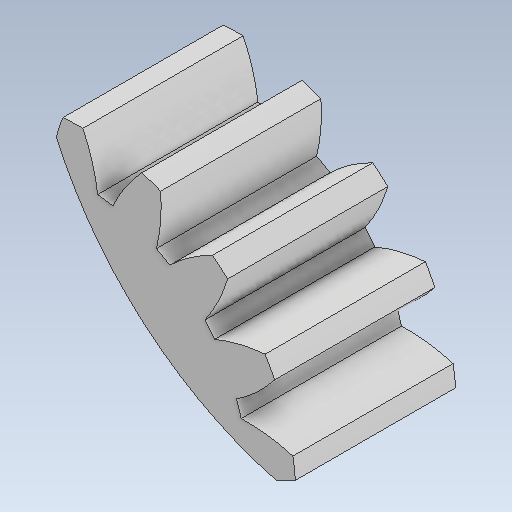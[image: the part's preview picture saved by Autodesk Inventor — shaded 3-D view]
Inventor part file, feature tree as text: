
AUTODESK INVENTOR PART (.ipt)
format: ipt  version: 2020 (Build 240168000, 168)  size: 285,696 bytes
history: native  units: mm
features: other x8, extrude x4, reference x4, sketch x3
ambient origin geometry x8: Origin, YZ Plane, XZ Plane, XY Plane, X Axis, Y Axis, Z Axis, Center Point
bodies: Body1 (feature_tree)
feature tree (19):
  other  "Bryła1"
  sketch  "Szkic1"
  extrude  "Wyciągnięcie proste1"  Depth=30.0mm
  extrude  "Wyciągnięcie proste2"  Depth=3.0mm TaperAngle=0.0deg
  extrude  "Wyciągnięcie proste3"  Depth=0.25mm
  extrude  "Wyciągnięcie proste5"  Depth=1.5mm TaperAngle=0.0deg
  reference  "Odniesienie1"
  reference  "Odniesienie2"
  reference  "Odniesienie3"
  sketch  "Szkic2"
  sketch  "Szkic4"
  reference  "Odniesienie4"
  other  "<userpath>\Desktop\3d\scanning-robot\Assembly1.iam"
  other  "Assembly1.iam"
  other  "Tower Pro MG90S Micro servo:2"
  other  "Цилиндрическое зубчатое зацепление:5"
  other  "Цилиндрическое зубчатое зацепление2:1"
  other  "<userpath>\Desktop\ScanBot\3d-model\Assembly1.iam"
  other  "Przekładnie walcowe:2"
